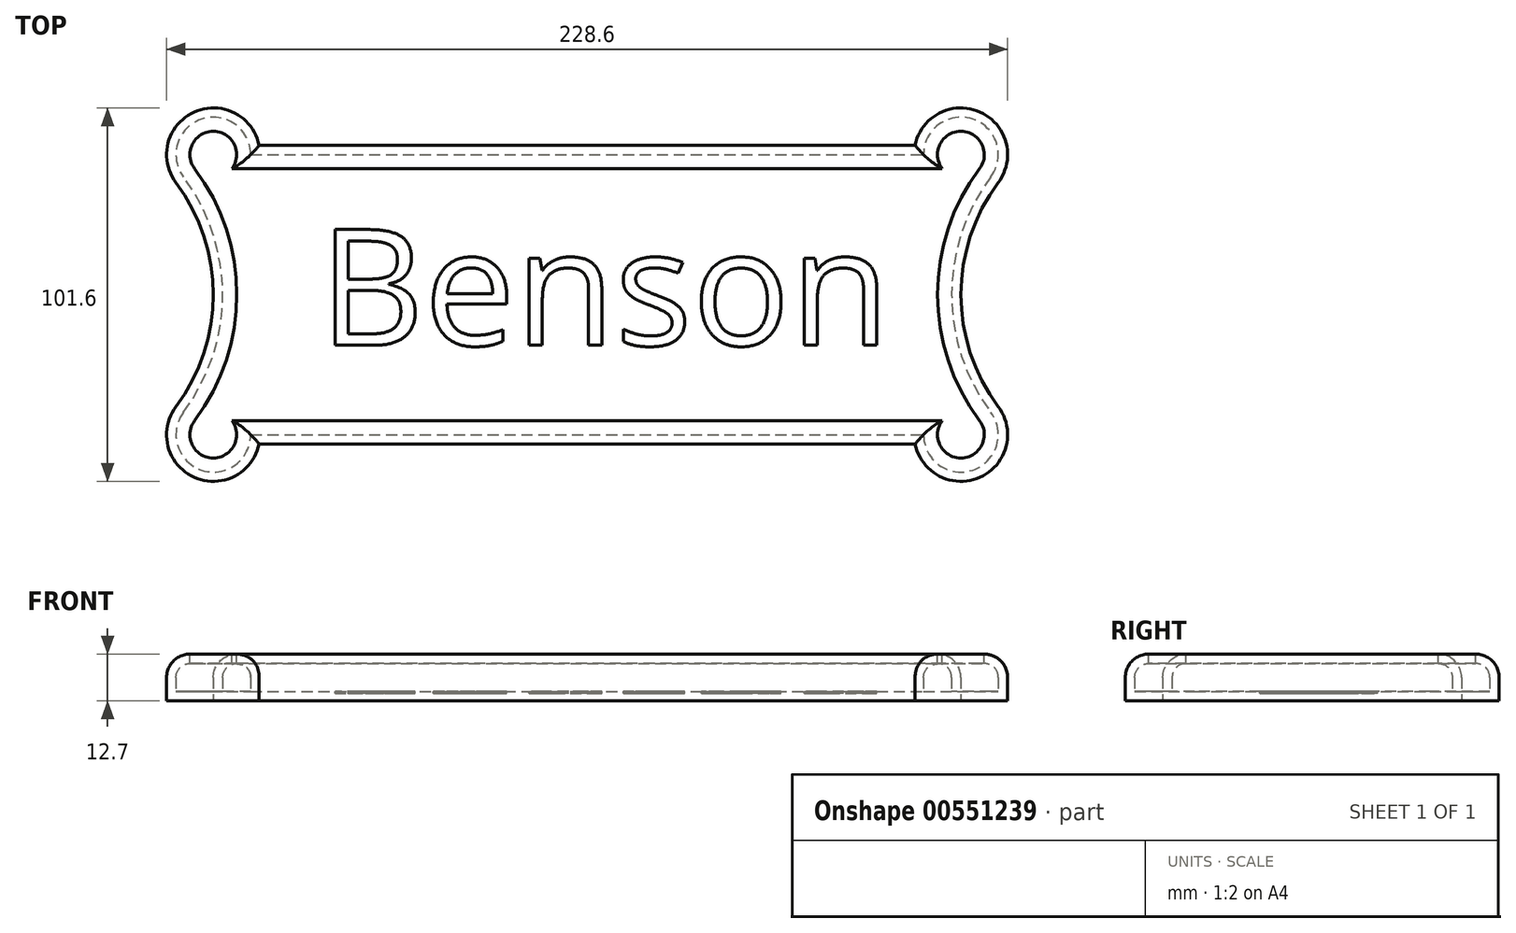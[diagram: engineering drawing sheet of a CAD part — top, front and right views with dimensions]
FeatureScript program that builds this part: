
annotation { "Feature Type Name" : "Feature", "Feature Type Description" : "" }
export const myFeature = defineFeature(function(context is Context, id is Id, definition is map)
    precondition{}
    {
        {
            var Q0;
            Q0=qCreatedBy(makeId("Top.planeOp"),FACE);
            var sketch = newSketch(context, id + "F0", { "sketchPlane" : qUnion([Q0])});
            skArc(sketch, "E0", {"start": v(163.38, 13.75) * mm, "mid": v(158.43, 32.96) * mm, "end": v(140.78, 23.9) * mm});
            skLineSegment(sketch, "E1", {"start": v(153.22, -16.73) * mm, "end": v(-53.58, -16.73) * mm, "construction": true});
            skLineSegment(sketch, "E2", {"start": v(51.62, 21.37) * mm, "end": v(51.62, -50.55) * mm, "construction": true});
            skArc(sketch, "E3.MirrorC", {"start": v(163.38, -47.2) * mm, "mid": v(158.43, -66.42) * mm, "end": v(140.78, -57.36) * mm});
            skArc(sketch, "E4", {"start": v(163.38, 13.75) * mm, "mid": v(153.22, -16.73) * mm, "end": v(163.38, -47.2) * mm});
            skArc(sketch, "E5.MirrorC", {"start": v(-60.14, 13.75) * mm, "mid": v(-55.18, 32.95) * mm, "end": v(-37.53, 23.9) * mm});
            skArc(sketch, "E6.MirrorCS", {"start": v(-60.14, 13.75) * mm, "mid": v(-49.98, -16.73) * mm, "end": v(-60.13, -47.21) * mm});
            skArc(sketch, "E7.MirrorC", {"start": v(-60.13, -47.21) * mm, "mid": v(-55.17, -66.42) * mm, "end": v(-37.53, -57.36) * mm});
            skLineSegment(sketch, "E8", {"start": v(-37.53, 23.9) * mm, "end": v(140.78, 23.9) * mm});
            skLineSegment(sketch, "E9.MirrorCS", {"start": v(-37.53, -57.36) * mm, "end": v(140.78, -57.36) * mm});
            skSolve(sketch);
        }
        {
            var Q0;
            Q0=makeQuery(id+"F0.imprint","IMPRINT",FACE,{"disambiguationData":[TD([[makeQuery(id+"F0.imprint","IMPRINT",EDGE,{"derivedFrom":sQuery(id+"F0.wireOp",EDGE,"E0")}),1.0]])]});
            extrude(context, id + "F1", {"entities" : qUnion([Q0]), "endBound" : BoundingType.SYMMETRIC, "depth" : 12.7 * mm, "offsetDistance" : 25.4 * mm});
        }
        {
            var Q0;
            Q0=makeQuery(id+"F1.opExtrude","CAP_FACE",FACE,{"disambiguationData":[OSD([sQuery(id+"F0.wireOp",EDGE,"E0"),sQuery(id+"F0.wireOp",EDGE,"E3.MirrorC"),sQuery(id+"F0.wireOp",EDGE,"E4"),sQuery(id+"F0.wireOp",EDGE,"E5.MirrorC"),sQuery(id+"F0.wireOp",EDGE,"E6.MirrorCS"),sQuery(id+"F0.wireOp",EDGE,"E7.MirrorC"),sQuery(id+"F0.wireOp",EDGE,"E8"),sQuery(id+"F0.wireOp",EDGE,"E9.MirrorCS")])],"isStart":false});
            fillet(context, id + "F2", {"entities" : qUnion([Q0]), "radius" : 6.35 * mm, "tangentPropagation" : true, "allowEdgeOverflow" : false});
        }
        {
            var Q0;
            Q0=makeQuery(id+"F1.opExtrude","CAP_FACE",FACE,{"disambiguationData":[OSD([sQuery(id+"F0.wireOp",EDGE,"E0"),sQuery(id+"F0.wireOp",EDGE,"E3.MirrorC"),sQuery(id+"F0.wireOp",EDGE,"E4"),sQuery(id+"F0.wireOp",EDGE,"E5.MirrorC"),sQuery(id+"F0.wireOp",EDGE,"E6.MirrorCS"),sQuery(id+"F0.wireOp",EDGE,"E7.MirrorC"),sQuery(id+"F0.wireOp",EDGE,"E8"),sQuery(id+"F0.wireOp",EDGE,"E9.MirrorCS")])],"isStart":false});
            shell(context, id + "F3", {"entities" : qUnion([Q0]), "thickness" : 2.54 * mm});
        }
        {
            var Q0;
            Q0=makeQuery(id+"F3.opShell","OFFSET_FACE",FACE,{"disambiguationData":[OSD([sQuery(id+"F0.wireOp",EDGE,"E0"),sQuery(id+"F0.wireOp",EDGE,"E3.MirrorC"),sQuery(id+"F0.wireOp",EDGE,"E4"),sQuery(id+"F0.wireOp",EDGE,"E5.MirrorC"),sQuery(id+"F0.wireOp",EDGE,"E6.MirrorCS"),sQuery(id+"F0.wireOp",EDGE,"E7.MirrorC"),sQuery(id+"F0.wireOp",EDGE,"E8"),sQuery(id+"F0.wireOp",EDGE,"E9.MirrorCS")])]});
            var sketch = newSketch(context, id + "F4", { "sketchPlane" : qUnion([Q0])});
            skText(sketch, "E10", { "text": "Benson", "fontName": "OpenSans-Regular.ttf"});
            const initialGuessF4  = {"E10": [-0.02123, -0.0305, 1, 0, 0.03175]};
            skSetInitialGuess(sketch, initialGuessF4);
            skSolve(sketch);
        }
        {
            var Q0;
            Q0 = qSketchRegion(id + "F4", true);
            extrude(context, id + "F5", {"entities" : qUnion([Q0]), "operationType" : NewBodyOperationType.REMOVE, "oppositeDirection" : true, "depth" : 0.5 * mm, "offsetDistance" : 25.4 * mm});
        }
    });
